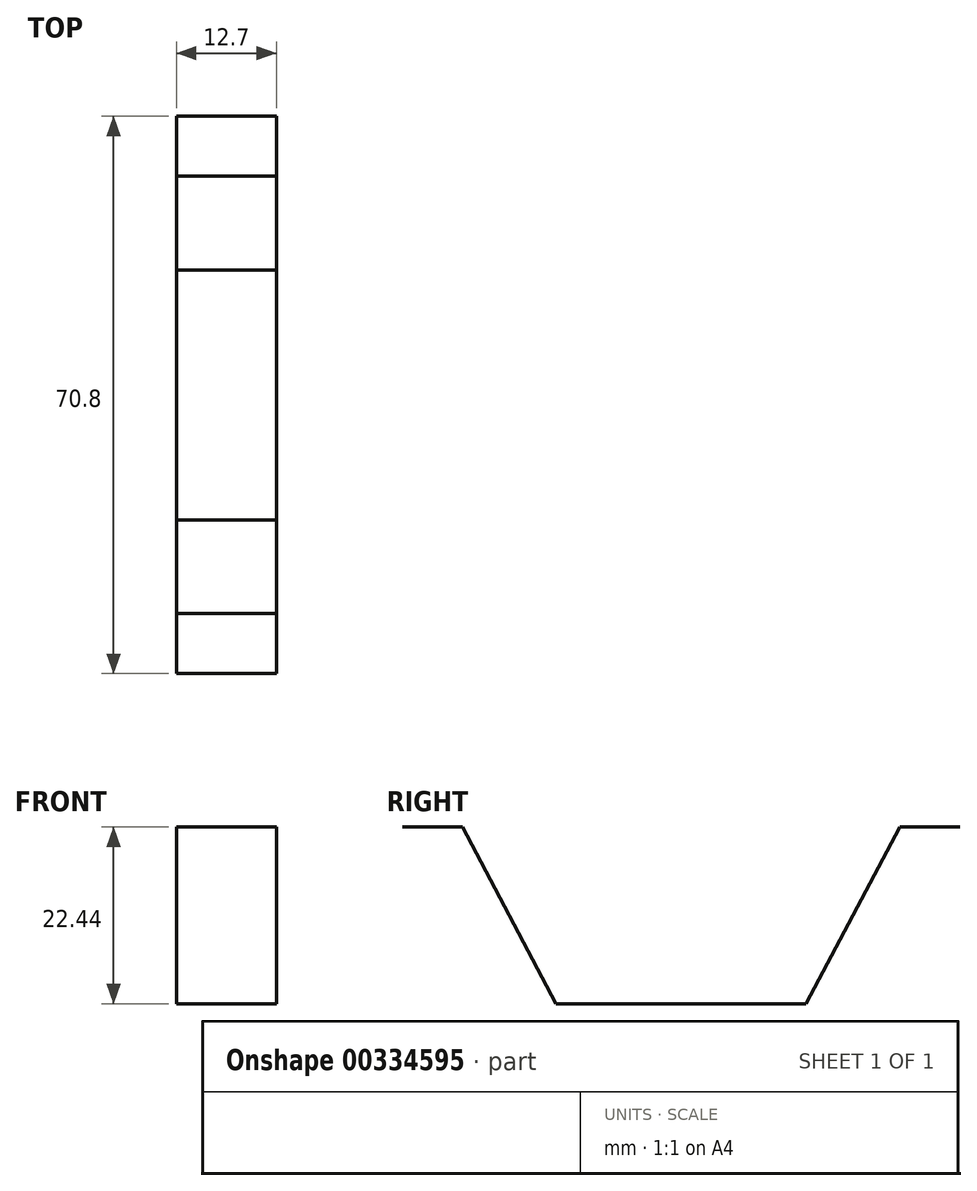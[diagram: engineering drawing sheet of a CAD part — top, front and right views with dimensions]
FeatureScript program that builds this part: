
annotation { "Feature Type Name" : "Feature", "Feature Type Description" : "" }
export const myFeature = defineFeature(function(context is Context, id is Id, definition is map)
    precondition{}
    {
        {
            var Q0;
            Q0=qCreatedBy(makeId("Right.planeOp"),FACE);
            var sketch = newSketch(context, id + "F0", { "sketchPlane" : qUnion([Q0])});
            skLineSegment(sketch, "E0", {"start": v(0, 0) * mm, "end": v(15.88, 0) * mm});
            skLineSegment(sketch, "E1", {"start": v(15.88, 0) * mm, "end": v(27.78, 22.44) * mm});
            skLineSegment(sketch, "E2", {"start": v(27.78, 22.44) * mm, "end": v(35.4, 22.44) * mm});
            skLineSegment(sketch, "E3", {"start": v(0, 0) * mm, "end": v(0, 19.77) * mm, "construction": true});
            skLineSegment(sketch, "E4.MirrorCS", {"start": v(0, 0) * mm, "end": v(-15.88, 0) * mm});
            skLineSegment(sketch, "E5.MirrorCS", {"start": v(-15.88, 0) * mm, "end": v(-27.78, 22.44) * mm});
            skLineSegment(sketch, "E6.MirrorCS", {"start": v(-27.78, 22.44) * mm, "end": v(-35.4, 22.44) * mm});
            skSolve(sketch);
        }
        {
            var Q0;
            Q0 = qSketchRegion(id + "F0", true);
            var Q1;
            Q1=sQuery(id+"F0.wireOp",EDGE,"E5.MirrorCS");
            var Q2;
            Q2=sQuery(id+"F0.wireOp",EDGE,"E6.MirrorCS");
            var Q3;
            Q3=sQuery(id+"F0.wireOp",EDGE,"E4.MirrorCS");
            var Q4;
            Q4=sQuery(id+"F0.wireOp",EDGE,"E0");
            var Q5;
            Q5=sQuery(id+"F0.wireOp",EDGE,"E1");
            var Q6;
            Q6=sQuery(id+"F0.wireOp",EDGE,"E2");
            extrude(context, id + "F1", {"entities" : qUnion([Q0]), "bodyType" : ToolBodyType.SURFACE, "operationType" : NewBodyOperationType.ADD, "surfaceEntities" : qUnion([Q1, Q2, Q3, Q4, Q5, Q6]), "depth" : 12.7 * mm});
        }
    });
